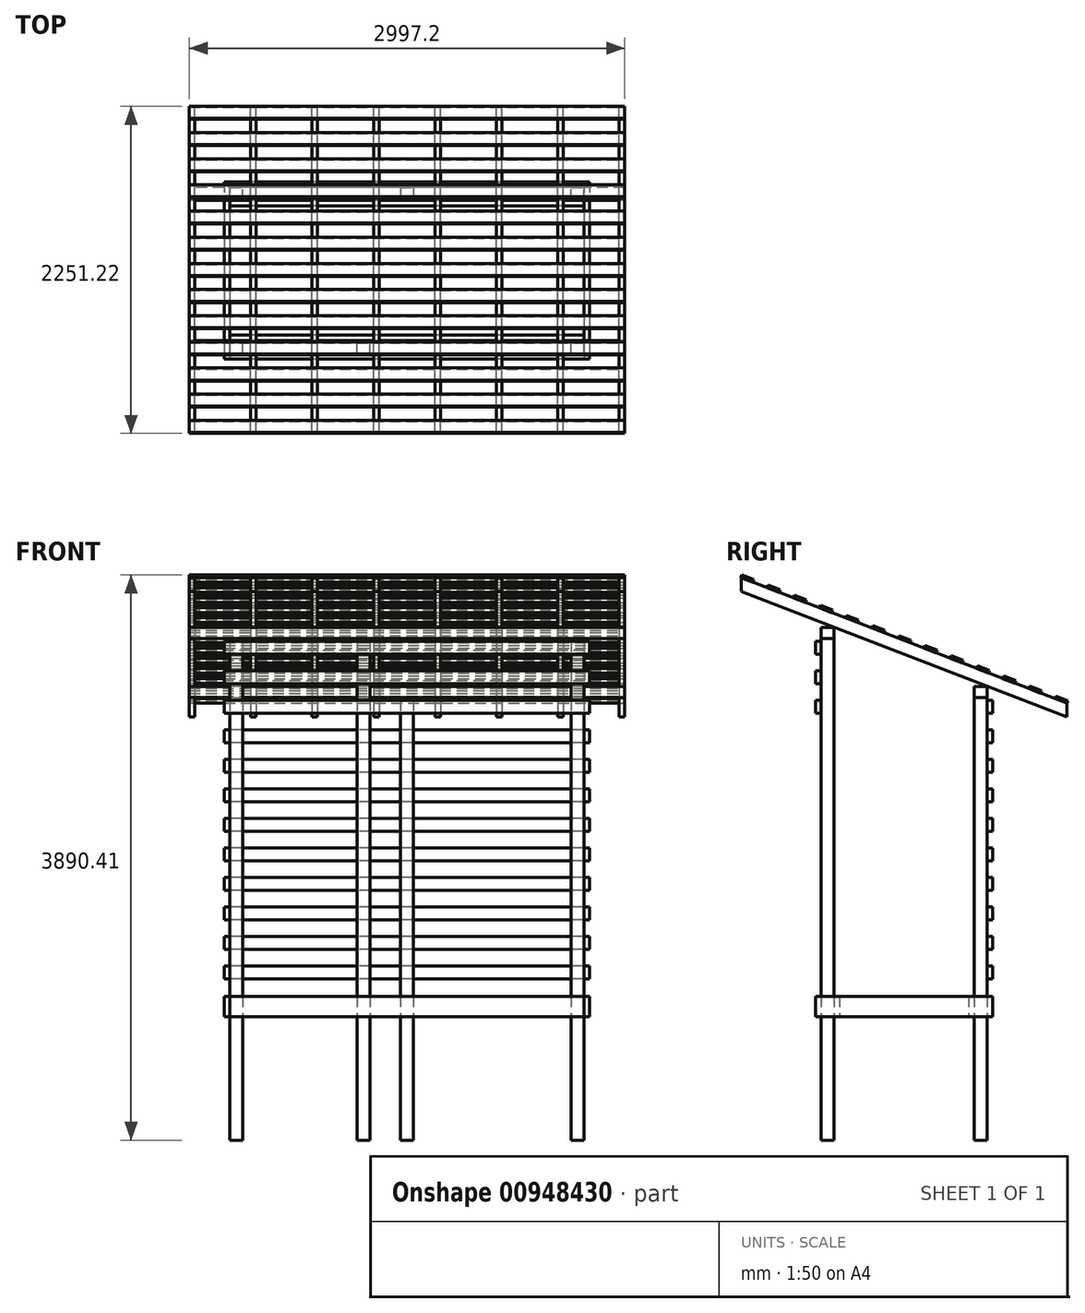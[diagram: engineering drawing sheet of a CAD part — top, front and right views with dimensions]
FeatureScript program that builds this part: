
annotation { "Feature Type Name" : "Feature", "Feature Type Description" : "" }
export const myFeature = defineFeature(function(context is Context, id is Id, definition is map)
    precondition{}
    {
        {
            var Q0;
            Q0=qCreatedBy(makeId("Top.planeOp"),FACE);
            var sketch = newSketch(context, id + "F0", { "sketchPlane" : qUnion([Q0])});
            skLineSegment(sketch, "E0.bottom", {"start": v(0, 0) * mm, "end": v(88.9, 0) * mm});
            skLineSegment(sketch, "E0.top", {"start": v(0, 88.9) * mm, "end": v(88.9, 88.9) * mm});
            skLineSegment(sketch, "E0.left", {"start": v(0, 0) * mm, "end": v(0, 88.9) * mm});
            skLineSegment(sketch, "E0.right", {"start": v(88.9, 0) * mm, "end": v(88.9, 88.9) * mm});
            skLineSegment(sketch, "E1.bottom", {"start": v(2349.5, 0) * mm, "end": v(2438.4, 0) * mm});
            skLineSegment(sketch, "E1.top", {"start": v(2349.5, 88.9) * mm, "end": v(2438.4, 88.9) * mm});
            skLineSegment(sketch, "E1.left", {"start": v(2349.5, 0) * mm, "end": v(2349.5, 88.9) * mm});
            skLineSegment(sketch, "E1.right", {"start": v(2438.4, 0) * mm, "end": v(2438.4, 88.9) * mm});
            skLineSegment(sketch, "E2.bottom", {"start": v(0, 1054.1) * mm, "end": v(88.9, 1054.1) * mm});
            skLineSegment(sketch, "E2.top", {"start": v(0, 1143) * mm, "end": v(88.9, 1143) * mm});
            skLineSegment(sketch, "E2.left", {"start": v(0, 1054.1) * mm, "end": v(0, 1143) * mm});
            skLineSegment(sketch, "E2.right", {"start": v(88.9, 1054.1) * mm, "end": v(88.9, 1143) * mm});
            skLineSegment(sketch, "E3.bottom", {"start": v(2349.5, 1054.1) * mm, "end": v(2438.4, 1054.1) * mm});
            skLineSegment(sketch, "E3.top", {"start": v(2349.5, 1143) * mm, "end": v(2438.4, 1143) * mm});
            skLineSegment(sketch, "E3.left", {"start": v(2349.5, 1054.1) * mm, "end": v(2349.5, 1143) * mm});
            skLineSegment(sketch, "E3.right", {"start": v(2438.4, 1054.1) * mm, "end": v(2438.4, 1143) * mm});
            skLineSegment(sketch, "E4.bottom", {"start": v(876.3, 0) * mm, "end": v(965.2, 0) * mm});
            skLineSegment(sketch, "E4.top", {"start": v(876.3, 88.9) * mm, "end": v(965.2, 88.9) * mm});
            skLineSegment(sketch, "E4.left", {"start": v(876.3, 0) * mm, "end": v(876.3, 88.9) * mm});
            skLineSegment(sketch, "E4.right", {"start": v(965.2, 0) * mm, "end": v(965.2, 88.9) * mm});
            skLineSegment(sketch, "E5.bottom", {"start": v(1174.75, 1143) * mm, "end": v(1263.65, 1143) * mm});
            skLineSegment(sketch, "E5.top", {"start": v(1174.75, 1054.1) * mm, "end": v(1263.65, 1054.1) * mm});
            skLineSegment(sketch, "E5.left", {"start": v(1174.75, 1143) * mm, "end": v(1174.75, 1054.1) * mm});
            skLineSegment(sketch, "E5.right", {"start": v(1263.65, 1143) * mm, "end": v(1263.65, 1054.1) * mm});
            skSolve(sketch);
        }
        {
            var Q0;
            Q0 = qSketchRegion(id + "F0", true);
            var Q1;
            Q1 = qConstructionFilter(qBodyType(qCreatedBy(id + "F0" ,EDGE), BodyType.WIRE), ConstructionObject.NO);
            extrude(context, id + "F1", {"entities" : qUnion([Q0]), "surfaceEntities" : qUnion([Q1]), "depth" : 2667 * mm, "offsetDistance" : 25.4 * mm, "hasSecondDirection" : true, "secondDirectionOppositeDirection" : true, "secondDirectionDepth" : 990.6 * mm});
        }
        {
            var Q0;
            Q0=qCreatedBy(makeId("Right.planeOp"),FACE);
            var sketch = newSketch(context, id + "F2", { "sketchPlane" : qUnion([Q0])});
            skLineSegment(sketch, "E6.bottom", {"start": v(0, 0) * mm, "end": v(-38.1, 0) * mm});
            skLineSegment(sketch, "E6.top", {"start": v(0, -139.7) * mm, "end": v(-38.1, -139.7) * mm});
            skLineSegment(sketch, "E6.left", {"start": v(0, 0) * mm, "end": v(0, -139.7) * mm});
            skLineSegment(sketch, "E6.right", {"start": v(-38.1, 0) * mm, "end": v(-38.1, -139.7) * mm});
            skLineSegment(sketch, "E7.bottom", {"start": v(1143, 0) * mm, "end": v(1181.1, 0) * mm});
            skLineSegment(sketch, "E7.top", {"start": v(1143, -139.7) * mm, "end": v(1181.1, -139.7) * mm});
            skLineSegment(sketch, "E7.left", {"start": v(1143, 0) * mm, "end": v(1143, -139.7) * mm});
            skLineSegment(sketch, "E7.right", {"start": v(1181.1, 0) * mm, "end": v(1181.1, -139.7) * mm});
            skLineSegment(sketch, "E8.bottom", {"start": v(1054.1, 0) * mm, "end": v(1016, 0) * mm});
            skLineSegment(sketch, "E8.top", {"start": v(1054.1, -139.7) * mm, "end": v(1016, -139.7) * mm});
            skLineSegment(sketch, "E8.left", {"start": v(1054.1, 0) * mm, "end": v(1054.1, -139.7) * mm});
            skLineSegment(sketch, "E8.right", {"start": v(1016, 0) * mm, "end": v(1016, -139.7) * mm});
            skLineSegment(sketch, "E9.bottom", {"start": v(127, 0) * mm, "end": v(88.9, 0) * mm});
            skLineSegment(sketch, "E9.top", {"start": v(127, -139.7) * mm, "end": v(88.9, -139.7) * mm});
            skLineSegment(sketch, "E9.left", {"start": v(127, 0) * mm, "end": v(127, -139.7) * mm});
            skLineSegment(sketch, "E9.right", {"start": v(88.9, 0) * mm, "end": v(88.9, -139.7) * mm});
            skSolve(sketch);
        }
        {
            var Q0;
            Q0 = qSketchRegion(id + "F2", true);
            extrude(context, id + "F3", {"entities" : qUnion([Q0]), "depth" : 2438.4 * mm, "offsetDistance" : 25.4 * mm});
        }
        {
            var Q0;
            Q0=makeQuery(id+"F3.opExtrude","SWEPT_FACE",FACE,{"disambiguationData":[OSD([sQuery(id+"F2.wireOp",EDGE,"E6.right")])]});
            var sketch = newSketch(context, id + "F4", { "sketchPlane" : qUnion([Q0])});
            skLineSegment(sketch, "E10.bottom", {"start": v(0, 0) * mm, "end": v(-38.1, 0) * mm});
            skLineSegment(sketch, "E10.top", {"start": v(0, -139.7) * mm, "end": v(-38.1, -139.7) * mm});
            skLineSegment(sketch, "E10.left", {"start": v(0, 0) * mm, "end": v(0, -139.7) * mm});
            skLineSegment(sketch, "E10.right", {"start": v(-38.1, 0) * mm, "end": v(-38.1, -139.7) * mm});
            skLineSegment(sketch, "E11.bottom", {"start": v(2476.5, 0) * mm, "end": v(2438.4, 0) * mm});
            skLineSegment(sketch, "E11.top", {"start": v(2476.5, -139.7) * mm, "end": v(2438.4, -139.7) * mm});
            skLineSegment(sketch, "E11.left", {"start": v(2476.5, 0) * mm, "end": v(2476.5, -139.7) * mm});
            skLineSegment(sketch, "E11.right", {"start": v(2438.4, 0) * mm, "end": v(2438.4, -139.7) * mm});
            skSolve(sketch);
        }
        {
            var Q0;
            Q0 = qSketchRegion(id + "F4", true);
            extrude(context, id + "F5", {"entities" : qUnion([Q0]), "oppositeDirection" : true, "depth" : 1219.2 * mm, "offsetDistance" : 25.4 * mm});
        }
        {
            var Q0;
            Q0=makeQuery(id+"F5.opExtrude","SWEPT_FACE",FACE,{"disambiguationData":[OSD([sQuery(id+"F4.wireOp",EDGE,"E10.right")])]});
            var sketch = newSketch(context, id + "F6", { "sketchPlane" : qUnion([Q0])});
            skLineSegment(sketch, "E12.bottom", {"start": v(-591.38, 2057.4) * mm, "end": v(-1626.38, 2057.4) * mm});
            skLineSegment(sketch, "E12.top", {"start": v(-591.38, 3060.64) * mm, "end": v(-1626.38, 3060.64) * mm});
            skLineSegment(sketch, "E12.left", {"start": v(-591.38, 2057.4) * mm, "end": v(-591.38, 3060.64) * mm});
            skLineSegment(sketch, "E12.right", {"start": v(-1626.38, 2057.4) * mm, "end": v(-1626.38, 3060.64) * mm});
            skLineSegment(sketch, "E13.bottom", {"start": v(182.21, 2463.8) * mm, "end": v(-373.83, 2463.8) * mm});
            skLineSegment(sketch, "E13.top", {"start": v(182.21, 2900.6) * mm, "end": v(-373.83, 2900.6) * mm});
            skLineSegment(sketch, "E13.left", {"start": v(182.21, 2463.8) * mm, "end": v(182.21, 2900.6) * mm});
            skLineSegment(sketch, "E13.right", {"start": v(-373.83, 2463.8) * mm, "end": v(-373.83, 2900.6) * mm});
            skSolve(sketch);
        }
        {
            var Q0;
            Q0 = qSketchRegion(id + "F6", true);
            extrude(context, id + "F7", {"entities" : qUnion([Q0]), "operationType" : NewBodyOperationType.REMOVE, "oppositeDirection" : true, "depth" : 2540 * mm, "offsetDistance" : 25.4 * mm});
        }
        {
            var Q0;
            Q0=makeQuery(id+"F1.opExtrude","SWEPT_FACE",FACE,{"disambiguationData":[OSD([sQuery(id+"F0.wireOp",EDGE,"E2.left")])]});
            cPlane(context, id + "F8", {"entities" : qUnion([Q0]), "cplaneType" : CPlaneType.OFFSET, "offset" : 279.4 * mm, "width" : 152.4 * mm, "height" : 152.4 * mm});
        }
        {
            var Q0;
            Q0=makeQuery(id+"F1.opExtrude","SWEPT_FACE",FACE,{"disambiguationData":[OSD([sQuery(id+"F0.wireOp",EDGE,"E3.right")])]});
            cPlane(context, id + "F9", {"entities" : qUnion([Q0]), "cplaneType" : CPlaneType.OFFSET, "offset" : 279.4 * mm, "width" : 152.4 * mm, "height" : 152.4 * mm});
        }
        {
            var Q0;
            Q0=qCreatedBy(id+"F8.planeOp",FACE);
            var sketch = newSketch(context, id + "F10", { "sketchPlane" : qUnion([Q0])});
            skLineSegment(sketch, "E14.bottom", {"start": v(-1143, 2133.6) * mm, "end": v(-1054.1, 2133.6) * mm});
            skLineSegment(sketch, "E14.top", {"start": v(-1143, 2095.5) * mm, "end": v(-1054.1, 2095.5) * mm});
            skLineSegment(sketch, "E14.left", {"start": v(-1143, 2133.6) * mm, "end": v(-1143, 2095.5) * mm});
            skLineSegment(sketch, "E14.right", {"start": v(-1054.1, 2133.6) * mm, "end": v(-1054.1, 2095.5) * mm});
            skLineSegment(sketch, "E15.top", {"start": v(-1143, 2057.4) * mm, "end": v(-1054.1, 2057.4) * mm});
            skLineSegment(sketch, "E15.left", {"start": v(-1143, 2095.5) * mm, "end": v(-1143, 2057.4) * mm});
            skLineSegment(sketch, "E15.right", {"start": v(-1054.1, 2095.5) * mm, "end": v(-1054.1, 2057.4) * mm});
            skLineSegment(sketch, "E16.bottom", {"start": v(0, 2540) * mm, "end": v(-88.9, 2540) * mm});
            skLineSegment(sketch, "E16.top", {"start": v(0, 2501.9) * mm, "end": v(-88.9, 2501.9) * mm});
            skLineSegment(sketch, "E16.left", {"start": v(0, 2540) * mm, "end": v(0, 2501.9) * mm});
            skLineSegment(sketch, "E16.right", {"start": v(-88.9, 2540) * mm, "end": v(-88.9, 2501.9) * mm});
            skLineSegment(sketch, "E17.top", {"start": v(0, 2463.8) * mm, "end": v(-88.9, 2463.8) * mm});
            skLineSegment(sketch, "E17.left", {"start": v(0, 2501.9) * mm, "end": v(0, 2463.8) * mm});
            skLineSegment(sketch, "E17.right", {"start": v(-88.9, 2501.9) * mm, "end": v(-88.9, 2463.8) * mm});
            skSolve(sketch);
        }
        {
            var Q0;
            Q0 = qSketchRegion(id + "F10", true);
            var Q1;
            Q1=qCreatedBy(id+"F9.planeOp",FACE);
            extrude(context, id + "F11", {"entities" : qUnion([Q0]), "endBound" : BoundingType.UP_TO_SURFACE, "oppositeDirection" : true, "depth" : 25.4 * mm, "endBoundEntityFace" : qUnion([Q1]), "offsetDistance" : 25.4 * mm});
        }
        {
            var Q0;
            Q0=makeQuery(id+"F11.opExtrude","CAP_VERTEX",VERTEX,{"disambiguationData":[OSD([sQuery(id+"F10.wireOp",EDGE,"E14.bottom"),sQuery(id+"F10.wireOp",EDGE,"E14.left"),sQuery(id+"F10.wireOp",EDGE,"E15.left")])],"isStart":false});
            var Q1;
            Q1=makeQuery(id+"F11.opExtrude","CAP_VERTEX",VERTEX,{"disambiguationData":[OSD([sQuery(id+"F10.wireOp",EDGE,"E14.bottom"),sQuery(id+"F10.wireOp",EDGE,"E14.left")])],"isStart":true});
            var Q2;
            Q2=makeQuery(id+"F11.opExtrude","CAP_VERTEX",VERTEX,{"disambiguationData":[OSD([sQuery(id+"F10.wireOp",EDGE,"E16.bottom"),sQuery(id+"F10.wireOp",EDGE,"E16.right")])],"isStart":true});
            cPlane(context, id + "F12", {"entities" : qUnion([Q0, Q1, Q2]), "cplaneType" : CPlaneType.THREE_POINT, "offset" : 25.4 * mm, "width" : 152.4 * mm, "height" : 152.4 * mm});
        }
        {
            var Q0;
            Q0=qCreatedBy(id+"F12.planeOp",FACE);
            var Q1;
            Q1=makeQuery(id+"F11.opExtrude","SWEPT_EDGE",EDGE,{"disambiguationData":[OSD([sQuery(id+"F10.wireOp",EDGE,"E16.bottom"),sQuery(id+"F10.wireOp",EDGE,"E16.right")])]});
            cPlane(context, id + "F13", {"entities" : qUnion([Q0, Q1]), "cplaneType" : CPlaneType.LINE_ANGLE, "offset" : 25.4 * mm, "angle" : 90 * degree, "oppositeDirection" : true, "width" : 152.4 * mm, "height" : 152.4 * mm});
        }
        {
            var Q0;
            Q0=qCreatedBy(id+"F13.planeOp",FACE);
            var sketch = newSketch(context, id + "F14", { "sketchPlane" : qUnion([Q0])});
            skLineSegment(sketch, "E18.bottom", {"start": v(-279.4, 2490.84) * mm, "end": v(-241.3, 2490.84) * mm});
            skLineSegment(sketch, "E18.top", {"start": v(-279.4, 2401.94) * mm, "end": v(-241.3, 2401.94) * mm});
            skLineSegment(sketch, "E18.left", {"start": v(-279.4, 2490.84) * mm, "end": v(-279.4, 2401.94) * mm});
            skLineSegment(sketch, "E18.right", {"start": v(-241.3, 2490.84) * mm, "end": v(-241.3, 2401.94) * mm});
            skLineSegment(sketch, "E19.1.0.0", {"start": v(181.36, 2490.84) * mm, "end": v(181.36, 2401.94) * mm});
            skLineSegment(sketch, "E19.1.0.1", {"start": v(143.26, 2490.84) * mm, "end": v(143.26, 2401.94) * mm});
            skLineSegment(sketch, "E19.1.0.2", {"start": v(143.26, 2490.84) * mm, "end": v(181.36, 2490.84) * mm});
            skLineSegment(sketch, "E19.1.0.3", {"start": v(143.26, 2401.94) * mm, "end": v(181.36, 2401.94) * mm});
            skLineSegment(sketch, "E19.2.0.0", {"start": v(604.01, 2490.84) * mm, "end": v(604.01, 2401.94) * mm});
            skLineSegment(sketch, "E19.2.0.1", {"start": v(565.91, 2490.84) * mm, "end": v(565.91, 2401.94) * mm});
            skLineSegment(sketch, "E19.2.0.2", {"start": v(565.91, 2490.84) * mm, "end": v(604.01, 2490.84) * mm});
            skLineSegment(sketch, "E19.2.0.3", {"start": v(565.91, 2401.94) * mm, "end": v(604.01, 2401.94) * mm});
            skLineSegment(sketch, "E19.3.0.0", {"start": v(1026.67, 2490.84) * mm, "end": v(1026.67, 2401.94) * mm});
            skLineSegment(sketch, "E19.3.0.1", {"start": v(988.57, 2490.84) * mm, "end": v(988.57, 2401.94) * mm});
            skLineSegment(sketch, "E19.3.0.2", {"start": v(988.57, 2490.84) * mm, "end": v(1026.67, 2490.84) * mm});
            skLineSegment(sketch, "E19.3.0.3", {"start": v(988.57, 2401.94) * mm, "end": v(1026.67, 2401.94) * mm});
            skLineSegment(sketch, "E19.4.0.0", {"start": v(1449.32, 2490.84) * mm, "end": v(1449.32, 2401.94) * mm});
            skLineSegment(sketch, "E19.4.0.1", {"start": v(1411.22, 2490.84) * mm, "end": v(1411.22, 2401.94) * mm});
            skLineSegment(sketch, "E19.4.0.2", {"start": v(1411.22, 2490.84) * mm, "end": v(1449.32, 2490.84) * mm});
            skLineSegment(sketch, "E19.4.0.3", {"start": v(1411.22, 2401.94) * mm, "end": v(1449.32, 2401.94) * mm});
            skLineSegment(sketch, "E19.5.0.0", {"start": v(1871.98, 2490.84) * mm, "end": v(1871.98, 2401.94) * mm});
            skLineSegment(sketch, "E19.5.0.1", {"start": v(1833.88, 2490.84) * mm, "end": v(1833.88, 2401.94) * mm});
            skLineSegment(sketch, "E19.5.0.2", {"start": v(1833.88, 2490.84) * mm, "end": v(1871.98, 2490.84) * mm});
            skLineSegment(sketch, "E19.5.0.3", {"start": v(1833.88, 2401.94) * mm, "end": v(1871.98, 2401.94) * mm});
            skLineSegment(sketch, "E19.6.0.0", {"start": v(2294.64, 2490.84) * mm, "end": v(2294.64, 2401.94) * mm});
            skLineSegment(sketch, "E19.6.0.1", {"start": v(2256.54, 2490.84) * mm, "end": v(2256.54, 2401.94) * mm});
            skLineSegment(sketch, "E19.6.0.2", {"start": v(2256.54, 2490.84) * mm, "end": v(2294.64, 2490.84) * mm});
            skLineSegment(sketch, "E19.6.0.3", {"start": v(2256.54, 2401.94) * mm, "end": v(2294.64, 2401.94) * mm});
            skLineSegment(sketch, "E19.7.0.0", {"start": v(2717.3, 2490.84) * mm, "end": v(2717.3, 2401.94) * mm});
            skLineSegment(sketch, "E19.7.0.1", {"start": v(2679.2, 2490.84) * mm, "end": v(2679.2, 2401.94) * mm});
            skLineSegment(sketch, "E19.7.0.2", {"start": v(2679.2, 2490.84) * mm, "end": v(2717.3, 2490.84) * mm});
            skLineSegment(sketch, "E19.7.0.3", {"start": v(2679.2, 2401.94) * mm, "end": v(2717.3, 2401.94) * mm});
            skLineSegment(sketch, "E19.direction1", {"start": v(-279.4, 2401.94) * mm, "end": v(143.26, 2401.94) * mm, "construction": true});
            skSolve(sketch);
        }
        {
            var Q0;
            Q0 = qSketchRegion(id + "F14", true);
            extrude(context, id + "F15", {"entities" : qUnion([Q0]), "depth" : 914.4 * mm, "offsetDistance" : 25.4 * mm, "hasSecondDirection" : true, "secondDirectionOppositeDirection" : true, "secondDirectionDepth" : 2032 * mm});
        }
        {
            var Q0;
            Q0=makeQuery(id+"F15.opExtrude","SWEPT_FACE",FACE,{"disambiguationData":[OSD([sQuery(id+"F14.wireOp",EDGE,"E19.7.0.0")])]});
            var sketch = newSketch(context, id + "F16", { "sketchPlane" : qUnion([Q0])});
            skLineSegment(sketch, "E20.0", {"start": v(-732.3, 2951.89) * mm, "end": v(2016.85, 1891.97) * mm, "construction": true});
            skLineSegment(sketch, "E21.0", {"start": v(-764.29, 2868.94) * mm, "end": v(1984.87, 1809.02) * mm, "construction": true});
            skLineSegment(sketch, "E22.0.1", {"start": v(1984.87, 1809.02) * mm, "end": v(-764.29, 2868.94) * mm, "construction": true});
            skLineSegment(sketch, "E23", {"start": v(-482.62, 3056.48) * mm, "end": v(-582.02, 2798.67) * mm, "construction": true});
            skLineSegment(sketch, "E24", {"start": v(1869.51, 2378.95) * mm, "end": v(1693.15, 1921.5) * mm, "construction": true});
            skLineSegment(sketch, "E25", {"start": v(-550.04, 2881.62) * mm, "end": v(-550.04, 1903.82) * mm, "construction": true});
            skLineSegment(sketch, "E26", {"start": v(1693.15, 1921.5) * mm, "end": v(1693.15, 2626.37) * mm, "construction": true});
            skLineSegment(sketch, "E27.bottom", {"start": v(-550.04, 1903.82) * mm, "end": v(-1357.61, 1903.82) * mm});
            skLineSegment(sketch, "E27.top", {"start": v(-550.04, 3436.76) * mm, "end": v(-1357.61, 3436.76) * mm});
            skLineSegment(sketch, "E27.left", {"start": v(-550.04, 1903.82) * mm, "end": v(-550.04, 3436.76) * mm});
            skLineSegment(sketch, "E27.right", {"start": v(-1357.61, 1903.82) * mm, "end": v(-1357.61, 3436.76) * mm});
            skLineSegment(sketch, "E28.bottom", {"start": v(1693.15, 2626.37) * mm, "end": v(2714.66, 2626.37) * mm});
            skLineSegment(sketch, "E28.top", {"start": v(1693.15, 1154.5) * mm, "end": v(2714.66, 1154.5) * mm});
            skLineSegment(sketch, "E28.left", {"start": v(1693.15, 2626.37) * mm, "end": v(1693.15, 1154.5) * mm});
            skLineSegment(sketch, "E28.right", {"start": v(2714.66, 2626.37) * mm, "end": v(2714.66, 1154.5) * mm});
            skSolve(sketch);
        }
        {
            var Q0;
            Q0 = qSketchRegion(id + "F16", true);
            extrude(context, id + "F17", {"entities" : qUnion([Q0]), "operationType" : NewBodyOperationType.REMOVE, "oppositeDirection" : true, "depth" : 3302 * mm, "offsetDistance" : 25.4 * mm});
        }
        {
            var Q0;
            Q0=makeQuery(id+"F15.opExtrude","SWEPT_FACE",FACE,{"disambiguationData":[OSD([sQuery(id+"F14.wireOp",EDGE,"E19.7.0.0")])]});
            var sketch = newSketch(context, id + "F18", { "sketchPlane" : qUnion([Q0])});
            skLineSegment(sketch, "E29", {"start": v(1693.15, 2016.77) * mm, "end": v(1610.2, 2048.75) * mm});
            skLineSegment(sketch, "E30", {"start": v(1610.2, 2048.75) * mm, "end": v(1617.05, 2066.53) * mm});
            skLineSegment(sketch, "E31", {"start": v(1617.05, 2066.53) * mm, "end": v(1700, 2034.55) * mm});
            skLineSegment(sketch, "E32", {"start": v(1693.15, 2016.77) * mm, "end": v(1700, 2034.55) * mm});
            skLineSegment(sketch, "E33", {"start": v(-550.04, 2881.62) * mm, "end": v(1693.15, 2016.77) * mm, "construction": true});
            skLineSegment(sketch, "E34.1.0.0", {"start": v(1513.03, 2086.21) * mm, "end": v(1430.08, 2118.2) * mm});
            skLineSegment(sketch, "E34.1.0.1", {"start": v(1436.93, 2135.97) * mm, "end": v(1519.88, 2103.99) * mm});
            skLineSegment(sketch, "E34.1.0.2", {"start": v(1430.08, 2118.2) * mm, "end": v(1436.93, 2135.97) * mm});
            skLineSegment(sketch, "E34.1.0.3", {"start": v(1513.03, 2086.21) * mm, "end": v(1519.88, 2103.99) * mm});
            skLineSegment(sketch, "E34.2.0.0", {"start": v(1332.9, 2155.65) * mm, "end": v(1249.96, 2187.63) * mm});
            skLineSegment(sketch, "E34.2.0.1", {"start": v(1256.81, 2205.4) * mm, "end": v(1339.76, 2173.43) * mm});
            skLineSegment(sketch, "E34.2.0.2", {"start": v(1249.96, 2187.63) * mm, "end": v(1256.81, 2205.4) * mm});
            skLineSegment(sketch, "E34.2.0.3", {"start": v(1332.9, 2155.65) * mm, "end": v(1339.76, 2173.43) * mm});
            skLineSegment(sketch, "E34.3.0.0", {"start": v(1152.8, 2225.1) * mm, "end": v(1069.84, 2257.07) * mm});
            skLineSegment(sketch, "E34.3.0.1", {"start": v(1076.7, 2274.85) * mm, "end": v(1159.64, 2242.87) * mm});
            skLineSegment(sketch, "E34.3.0.2", {"start": v(1069.84, 2257.07) * mm, "end": v(1076.7, 2274.85) * mm});
            skLineSegment(sketch, "E34.3.0.3", {"start": v(1152.8, 2225.1) * mm, "end": v(1159.64, 2242.87) * mm});
            skLineSegment(sketch, "E34.4.0.0", {"start": v(972.67, 2294.53) * mm, "end": v(889.72, 2326.52) * mm});
            skLineSegment(sketch, "E34.4.0.1", {"start": v(896.58, 2344.29) * mm, "end": v(979.53, 2312.3) * mm});
            skLineSegment(sketch, "E34.4.0.2", {"start": v(889.72, 2326.52) * mm, "end": v(896.58, 2344.29) * mm});
            skLineSegment(sketch, "E34.4.0.3", {"start": v(972.67, 2294.53) * mm, "end": v(979.53, 2312.3) * mm});
            skLineSegment(sketch, "E34.5.0.0", {"start": v(792.56, 2363.98) * mm, "end": v(709.6, 2395.96) * mm});
            skLineSegment(sketch, "E34.5.0.1", {"start": v(716.46, 2413.73) * mm, "end": v(799.4, 2381.75) * mm});
            skLineSegment(sketch, "E34.5.0.2", {"start": v(709.6, 2395.96) * mm, "end": v(716.46, 2413.73) * mm});
            skLineSegment(sketch, "E34.5.0.3", {"start": v(792.56, 2363.98) * mm, "end": v(799.4, 2381.75) * mm});
            skLineSegment(sketch, "E34.6.0.0", {"start": v(612.44, 2433.42) * mm, "end": v(529.49, 2465.4) * mm});
            skLineSegment(sketch, "E34.6.0.1", {"start": v(536.34, 2483.17) * mm, "end": v(619.3, 2451.2) * mm});
            skLineSegment(sketch, "E34.6.0.2", {"start": v(529.49, 2465.4) * mm, "end": v(536.34, 2483.17) * mm});
            skLineSegment(sketch, "E34.6.0.3", {"start": v(612.44, 2433.42) * mm, "end": v(619.3, 2451.2) * mm});
            skLineSegment(sketch, "E34.7.0.0", {"start": v(432.32, 2502.86) * mm, "end": v(349.37, 2534.84) * mm});
            skLineSegment(sketch, "E34.7.0.1", {"start": v(356.22, 2552.61) * mm, "end": v(439.17, 2520.63) * mm});
            skLineSegment(sketch, "E34.7.0.2", {"start": v(349.37, 2534.84) * mm, "end": v(356.22, 2552.61) * mm});
            skLineSegment(sketch, "E34.7.0.3", {"start": v(432.32, 2502.86) * mm, "end": v(439.17, 2520.63) * mm});
            skLineSegment(sketch, "E34.8.0.0", {"start": v(252.2, 2572.3) * mm, "end": v(169.25, 2604.28) * mm});
            skLineSegment(sketch, "E34.8.0.1", {"start": v(176.1, 2622.05) * mm, "end": v(259.05, 2590.07) * mm});
            skLineSegment(sketch, "E34.8.0.2", {"start": v(169.25, 2604.28) * mm, "end": v(176.1, 2622.05) * mm});
            skLineSegment(sketch, "E34.8.0.3", {"start": v(252.2, 2572.3) * mm, "end": v(259.05, 2590.07) * mm});
            skLineSegment(sketch, "E34.9.0.0", {"start": v(72.08, 2641.74) * mm, "end": v(-10.87, 2673.72) * mm});
            skLineSegment(sketch, "E34.9.0.1", {"start": v(-4.01, 2691.5) * mm, "end": v(78.94, 2659.51) * mm});
            skLineSegment(sketch, "E34.9.0.2", {"start": v(-10.87, 2673.72) * mm, "end": v(-4.01, 2691.5) * mm});
            skLineSegment(sketch, "E34.9.0.3", {"start": v(72.08, 2641.74) * mm, "end": v(78.94, 2659.51) * mm});
            skLineSegment(sketch, "E34.10.0.0", {"start": v(-108.03, 2711.18) * mm, "end": v(-190.98, 2743.16) * mm});
            skLineSegment(sketch, "E34.10.0.1", {"start": v(-184.13, 2760.93) * mm, "end": v(-101.18, 2728.95) * mm});
            skLineSegment(sketch, "E34.10.0.2", {"start": v(-190.98, 2743.16) * mm, "end": v(-184.13, 2760.93) * mm});
            skLineSegment(sketch, "E34.10.0.3", {"start": v(-108.03, 2711.18) * mm, "end": v(-101.18, 2728.95) * mm});
            skLineSegment(sketch, "E34.11.0.0", {"start": v(-288.15, 2780.62) * mm, "end": v(-371.1, 2812.6) * mm});
            skLineSegment(sketch, "E34.11.0.1", {"start": v(-364.25, 2830.37) * mm, "end": v(-281.3, 2798.4) * mm});
            skLineSegment(sketch, "E34.11.0.2", {"start": v(-371.1, 2812.6) * mm, "end": v(-364.25, 2830.37) * mm});
            skLineSegment(sketch, "E34.11.0.3", {"start": v(-288.15, 2780.62) * mm, "end": v(-281.3, 2798.4) * mm});
            skLineSegment(sketch, "E34.12.0.0", {"start": v(-468.27, 2850.06) * mm, "end": v(-551.22, 2882.04) * mm});
            skLineSegment(sketch, "E34.12.0.1", {"start": v(-544.37, 2899.81) * mm, "end": v(-461.42, 2867.83) * mm});
            skLineSegment(sketch, "E34.12.0.2", {"start": v(-551.22, 2882.04) * mm, "end": v(-544.37, 2899.81) * mm});
            skLineSegment(sketch, "E34.12.0.3", {"start": v(-468.27, 2850.06) * mm, "end": v(-461.42, 2867.83) * mm});
            skLineSegment(sketch, "E34.direction1", {"start": v(1610.2, 2048.75) * mm, "end": v(1430.08, 2118.2) * mm, "construction": true});
            skSolve(sketch);
        }
        {
            var Q0;
            Q0 = qSketchRegion(id + "F18", true);
            var Q1;
            Q1=makeQuery(id+"F15.opExtrude","SWEPT_FACE",FACE,{"disambiguationData":[OSD([sQuery(id+"F14.wireOp",EDGE,"E18.left")])]});
            extrude(context, id + "F19", {"entities" : qUnion([Q0]), "endBound" : BoundingType.UP_TO_SURFACE, "oppositeDirection" : true, "depth" : 25.4 * mm, "endBoundEntityFace" : qUnion([Q1]), "offsetDistance" : 25.4 * mm});
        }
        {
            var Q0;
            Q0=makeQuery(id+"F5.opExtrude","SWEPT_FACE",FACE,{"disambiguationData":[OSD([sQuery(id+"F4.wireOp",EDGE,"E10.right")])]});
            var sketch = newSketch(context, id + "F20", { "sketchPlane" : qUnion([Q0])});
            skLineSegment(sketch, "E35.bottom", {"start": v(-1181.1, 2038.35) * mm, "end": v(-1143, 2038.35) * mm});
            skLineSegment(sketch, "E35.top", {"start": v(-1181.1, 1949.45) * mm, "end": v(-1143, 1949.45) * mm});
            skLineSegment(sketch, "E35.left", {"start": v(-1181.1, 2038.35) * mm, "end": v(-1181.1, 1949.45) * mm});
            skLineSegment(sketch, "E35.right", {"start": v(-1143, 2038.35) * mm, "end": v(-1143, 1949.45) * mm});
            skLineSegment(sketch, "E36.bottom", {"start": v(38.1, 2038.35) * mm, "end": v(0, 2038.35) * mm});
            skLineSegment(sketch, "E36.top", {"start": v(38.1, 1949.45) * mm, "end": v(0, 1949.45) * mm});
            skLineSegment(sketch, "E36.left", {"start": v(38.1, 2038.35) * mm, "end": v(38.1, 1949.45) * mm});
            skLineSegment(sketch, "E36.right", {"start": v(0, 2038.35) * mm, "end": v(0, 1949.45) * mm});
            skLineSegment(sketch, "E37.0.1.0", {"start": v(-1181.1, 1835.15) * mm, "end": v(-1181.1, 1746.25) * mm});
            skLineSegment(sketch, "E37.0.1.1", {"start": v(-1143, 1835.15) * mm, "end": v(-1143, 1746.25) * mm});
            skLineSegment(sketch, "E37.0.1.2", {"start": v(-1181.1, 1835.15) * mm, "end": v(-1143, 1835.15) * mm});
            skLineSegment(sketch, "E37.0.1.3", {"start": v(-1181.1, 1746.25) * mm, "end": v(-1143, 1746.25) * mm});
            skLineSegment(sketch, "E37.0.2.0", {"start": v(-1181.1, 1631.95) * mm, "end": v(-1181.1, 1543.05) * mm});
            skLineSegment(sketch, "E37.0.2.1", {"start": v(-1143, 1631.95) * mm, "end": v(-1143, 1543.05) * mm});
            skLineSegment(sketch, "E37.0.2.2", {"start": v(-1181.1, 1631.95) * mm, "end": v(-1143, 1631.95) * mm});
            skLineSegment(sketch, "E37.0.2.3", {"start": v(-1181.1, 1543.05) * mm, "end": v(-1143, 1543.05) * mm});
            skLineSegment(sketch, "E37.0.3.0", {"start": v(-1181.1, 1428.75) * mm, "end": v(-1181.1, 1339.85) * mm});
            skLineSegment(sketch, "E37.0.3.1", {"start": v(-1143, 1428.75) * mm, "end": v(-1143, 1339.85) * mm});
            skLineSegment(sketch, "E37.0.3.2", {"start": v(-1181.1, 1428.75) * mm, "end": v(-1143, 1428.75) * mm});
            skLineSegment(sketch, "E37.0.3.3", {"start": v(-1181.1, 1339.85) * mm, "end": v(-1143, 1339.85) * mm});
            skLineSegment(sketch, "E37.0.4.0", {"start": v(-1181.1, 1225.55) * mm, "end": v(-1181.1, 1136.65) * mm});
            skLineSegment(sketch, "E37.0.4.1", {"start": v(-1143, 1225.55) * mm, "end": v(-1143, 1136.65) * mm});
            skLineSegment(sketch, "E37.0.4.2", {"start": v(-1181.1, 1225.55) * mm, "end": v(-1143, 1225.55) * mm});
            skLineSegment(sketch, "E37.0.4.3", {"start": v(-1181.1, 1136.65) * mm, "end": v(-1143, 1136.65) * mm});
            skLineSegment(sketch, "E37.0.5.0", {"start": v(-1181.1, 1022.35) * mm, "end": v(-1181.1, 933.45) * mm});
            skLineSegment(sketch, "E37.0.5.1", {"start": v(-1143, 1022.35) * mm, "end": v(-1143, 933.45) * mm});
            skLineSegment(sketch, "E37.0.5.2", {"start": v(-1181.1, 1022.35) * mm, "end": v(-1143, 1022.35) * mm});
            skLineSegment(sketch, "E37.0.5.3", {"start": v(-1181.1, 933.45) * mm, "end": v(-1143, 933.45) * mm});
            skLineSegment(sketch, "E37.0.6.0", {"start": v(-1181.1, 819.15) * mm, "end": v(-1181.1, 730.25) * mm});
            skLineSegment(sketch, "E37.0.6.1", {"start": v(-1143, 819.15) * mm, "end": v(-1143, 730.25) * mm});
            skLineSegment(sketch, "E37.0.6.2", {"start": v(-1181.1, 819.15) * mm, "end": v(-1143, 819.15) * mm});
            skLineSegment(sketch, "E37.0.6.3", {"start": v(-1181.1, 730.25) * mm, "end": v(-1143, 730.25) * mm});
            skLineSegment(sketch, "E37.0.7.0", {"start": v(-1181.1, 615.95) * mm, "end": v(-1181.1, 527.05) * mm});
            skLineSegment(sketch, "E37.0.7.1", {"start": v(-1143, 615.95) * mm, "end": v(-1143, 527.05) * mm});
            skLineSegment(sketch, "E37.0.7.2", {"start": v(-1181.1, 615.95) * mm, "end": v(-1143, 615.95) * mm});
            skLineSegment(sketch, "E37.0.7.3", {"start": v(-1181.1, 527.05) * mm, "end": v(-1143, 527.05) * mm});
            skLineSegment(sketch, "E37.0.8.0", {"start": v(-1181.1, 412.75) * mm, "end": v(-1181.1, 323.85) * mm});
            skLineSegment(sketch, "E37.0.8.1", {"start": v(-1143, 412.75) * mm, "end": v(-1143, 323.85) * mm});
            skLineSegment(sketch, "E37.0.8.2", {"start": v(-1181.1, 412.75) * mm, "end": v(-1143, 412.75) * mm});
            skLineSegment(sketch, "E37.0.8.3", {"start": v(-1181.1, 323.85) * mm, "end": v(-1143, 323.85) * mm});
            skLineSegment(sketch, "E37.0.9.0", {"start": v(-1181.1, 209.55) * mm, "end": v(-1181.1, 120.65) * mm});
            skLineSegment(sketch, "E37.0.9.1", {"start": v(-1143, 209.55) * mm, "end": v(-1143, 120.65) * mm});
            skLineSegment(sketch, "E37.0.9.2", {"start": v(-1181.1, 209.55) * mm, "end": v(-1143, 209.55) * mm});
            skLineSegment(sketch, "E37.0.9.3", {"start": v(-1181.1, 120.65) * mm, "end": v(-1143, 120.65) * mm});
            skLineSegment(sketch, "E37.1.1.0", {"start": v(-1181.1, 1835.15) * mm, "end": v(-1181.1, 1746.25) * mm});
            skLineSegment(sketch, "E37.1.1.1", {"start": v(-1143, 1835.15) * mm, "end": v(-1143, 1746.25) * mm});
            skLineSegment(sketch, "E37.1.1.2", {"start": v(-1181.1, 1835.15) * mm, "end": v(-1143, 1835.15) * mm});
            skLineSegment(sketch, "E37.1.1.3", {"start": v(-1181.1, 1746.25) * mm, "end": v(-1143, 1746.25) * mm});
            skLineSegment(sketch, "E37.1.2.0", {"start": v(-1181.1, 1631.95) * mm, "end": v(-1181.1, 1543.05) * mm});
            skLineSegment(sketch, "E37.1.2.1", {"start": v(-1143, 1631.95) * mm, "end": v(-1143, 1543.05) * mm});
            skLineSegment(sketch, "E37.1.2.2", {"start": v(-1181.1, 1631.95) * mm, "end": v(-1143, 1631.95) * mm});
            skLineSegment(sketch, "E37.1.2.3", {"start": v(-1181.1, 1543.05) * mm, "end": v(-1143, 1543.05) * mm});
            skLineSegment(sketch, "E37.1.3.0", {"start": v(-1181.1, 1428.75) * mm, "end": v(-1181.1, 1339.85) * mm});
            skLineSegment(sketch, "E37.1.3.1", {"start": v(-1143, 1428.75) * mm, "end": v(-1143, 1339.85) * mm});
            skLineSegment(sketch, "E37.1.3.2", {"start": v(-1181.1, 1428.75) * mm, "end": v(-1143, 1428.75) * mm});
            skLineSegment(sketch, "E37.1.3.3", {"start": v(-1181.1, 1339.85) * mm, "end": v(-1143, 1339.85) * mm});
            skLineSegment(sketch, "E37.1.4.0", {"start": v(-1181.1, 1225.55) * mm, "end": v(-1181.1, 1136.65) * mm});
            skLineSegment(sketch, "E37.1.4.1", {"start": v(-1143, 1225.55) * mm, "end": v(-1143, 1136.65) * mm});
            skLineSegment(sketch, "E37.1.4.2", {"start": v(-1181.1, 1225.55) * mm, "end": v(-1143, 1225.55) * mm});
            skLineSegment(sketch, "E37.1.4.3", {"start": v(-1181.1, 1136.65) * mm, "end": v(-1143, 1136.65) * mm});
            skLineSegment(sketch, "E37.1.5.0", {"start": v(-1181.1, 1022.35) * mm, "end": v(-1181.1, 933.45) * mm});
            skLineSegment(sketch, "E37.1.5.1", {"start": v(-1143, 1022.35) * mm, "end": v(-1143, 933.45) * mm});
            skLineSegment(sketch, "E37.1.5.2", {"start": v(-1181.1, 1022.35) * mm, "end": v(-1143, 1022.35) * mm});
            skLineSegment(sketch, "E37.1.5.3", {"start": v(-1181.1, 933.45) * mm, "end": v(-1143, 933.45) * mm});
            skLineSegment(sketch, "E37.1.6.0", {"start": v(-1181.1, 819.15) * mm, "end": v(-1181.1, 730.25) * mm});
            skLineSegment(sketch, "E37.1.6.1", {"start": v(-1143, 819.15) * mm, "end": v(-1143, 730.25) * mm});
            skLineSegment(sketch, "E37.1.6.2", {"start": v(-1181.1, 819.15) * mm, "end": v(-1143, 819.15) * mm});
            skLineSegment(sketch, "E37.1.6.3", {"start": v(-1181.1, 730.25) * mm, "end": v(-1143, 730.25) * mm});
            skLineSegment(sketch, "E37.1.7.0", {"start": v(-1181.1, 615.95) * mm, "end": v(-1181.1, 527.05) * mm});
            skLineSegment(sketch, "E37.1.7.1", {"start": v(-1143, 615.95) * mm, "end": v(-1143, 527.05) * mm});
            skLineSegment(sketch, "E37.1.7.2", {"start": v(-1181.1, 615.95) * mm, "end": v(-1143, 615.95) * mm});
            skLineSegment(sketch, "E37.1.7.3", {"start": v(-1181.1, 527.05) * mm, "end": v(-1143, 527.05) * mm});
            skLineSegment(sketch, "E37.1.8.0", {"start": v(-1181.1, 412.75) * mm, "end": v(-1181.1, 323.85) * mm});
            skLineSegment(sketch, "E37.1.8.1", {"start": v(-1143, 412.75) * mm, "end": v(-1143, 323.85) * mm});
            skLineSegment(sketch, "E37.1.8.2", {"start": v(-1181.1, 412.75) * mm, "end": v(-1143, 412.75) * mm});
            skLineSegment(sketch, "E37.1.8.3", {"start": v(-1181.1, 323.85) * mm, "end": v(-1143, 323.85) * mm});
            skLineSegment(sketch, "E37.1.9.0", {"start": v(-1181.1, 209.55) * mm, "end": v(-1181.1, 120.65) * mm});
            skLineSegment(sketch, "E37.1.9.1", {"start": v(-1143, 209.55) * mm, "end": v(-1143, 120.65) * mm});
            skLineSegment(sketch, "E37.1.9.2", {"start": v(-1181.1, 209.55) * mm, "end": v(-1143, 209.55) * mm});
            skLineSegment(sketch, "E37.1.9.3", {"start": v(-1181.1, 120.65) * mm, "end": v(-1143, 120.65) * mm});
            skLineSegment(sketch, "E37.2.1.0", {"start": v(-1181.1, 1835.15) * mm, "end": v(-1181.1, 1746.25) * mm});
            skLineSegment(sketch, "E37.2.1.1", {"start": v(-1143, 1835.15) * mm, "end": v(-1143, 1746.25) * mm});
            skLineSegment(sketch, "E37.2.1.2", {"start": v(-1181.1, 1835.15) * mm, "end": v(-1143, 1835.15) * mm});
            skLineSegment(sketch, "E37.2.1.3", {"start": v(-1181.1, 1746.25) * mm, "end": v(-1143, 1746.25) * mm});
            skLineSegment(sketch, "E37.2.2.0", {"start": v(-1181.1, 1631.95) * mm, "end": v(-1181.1, 1543.05) * mm});
            skLineSegment(sketch, "E37.2.2.1", {"start": v(-1143, 1631.95) * mm, "end": v(-1143, 1543.05) * mm});
            skLineSegment(sketch, "E37.2.2.2", {"start": v(-1181.1, 1631.95) * mm, "end": v(-1143, 1631.95) * mm});
            skLineSegment(sketch, "E37.2.2.3", {"start": v(-1181.1, 1543.05) * mm, "end": v(-1143, 1543.05) * mm});
            skLineSegment(sketch, "E37.2.3.0", {"start": v(-1181.1, 1428.75) * mm, "end": v(-1181.1, 1339.85) * mm});
            skLineSegment(sketch, "E37.2.3.1", {"start": v(-1143, 1428.75) * mm, "end": v(-1143, 1339.85) * mm});
            skLineSegment(sketch, "E37.2.3.2", {"start": v(-1181.1, 1428.75) * mm, "end": v(-1143, 1428.75) * mm});
            skLineSegment(sketch, "E37.2.3.3", {"start": v(-1181.1, 1339.85) * mm, "end": v(-1143, 1339.85) * mm});
            skLineSegment(sketch, "E37.2.4.0", {"start": v(-1181.1, 1225.55) * mm, "end": v(-1181.1, 1136.65) * mm});
            skLineSegment(sketch, "E37.2.4.1", {"start": v(-1143, 1225.55) * mm, "end": v(-1143, 1136.65) * mm});
            skLineSegment(sketch, "E37.2.4.2", {"start": v(-1181.1, 1225.55) * mm, "end": v(-1143, 1225.55) * mm});
            skLineSegment(sketch, "E37.2.4.3", {"start": v(-1181.1, 1136.65) * mm, "end": v(-1143, 1136.65) * mm});
            skLineSegment(sketch, "E37.2.5.0", {"start": v(-1181.1, 1022.35) * mm, "end": v(-1181.1, 933.45) * mm});
            skLineSegment(sketch, "E37.2.5.1", {"start": v(-1143, 1022.35) * mm, "end": v(-1143, 933.45) * mm});
            skLineSegment(sketch, "E37.2.5.2", {"start": v(-1181.1, 1022.35) * mm, "end": v(-1143, 1022.35) * mm});
            skLineSegment(sketch, "E37.2.5.3", {"start": v(-1181.1, 933.45) * mm, "end": v(-1143, 933.45) * mm});
            skLineSegment(sketch, "E37.2.6.0", {"start": v(-1181.1, 819.15) * mm, "end": v(-1181.1, 730.25) * mm});
            skLineSegment(sketch, "E37.2.6.1", {"start": v(-1143, 819.15) * mm, "end": v(-1143, 730.25) * mm});
            skLineSegment(sketch, "E37.2.6.2", {"start": v(-1181.1, 819.15) * mm, "end": v(-1143, 819.15) * mm});
            skLineSegment(sketch, "E37.2.6.3", {"start": v(-1181.1, 730.25) * mm, "end": v(-1143, 730.25) * mm});
            skLineSegment(sketch, "E37.2.7.0", {"start": v(-1181.1, 615.95) * mm, "end": v(-1181.1, 527.05) * mm});
            skLineSegment(sketch, "E37.2.7.1", {"start": v(-1143, 615.95) * mm, "end": v(-1143, 527.05) * mm});
            skLineSegment(sketch, "E37.2.7.2", {"start": v(-1181.1, 615.95) * mm, "end": v(-1143, 615.95) * mm});
            skLineSegment(sketch, "E37.2.7.3", {"start": v(-1181.1, 527.05) * mm, "end": v(-1143, 527.05) * mm});
            skLineSegment(sketch, "E37.2.8.0", {"start": v(-1181.1, 412.75) * mm, "end": v(-1181.1, 323.85) * mm});
            skLineSegment(sketch, "E37.2.8.1", {"start": v(-1143, 412.75) * mm, "end": v(-1143, 323.85) * mm});
            skLineSegment(sketch, "E37.2.8.2", {"start": v(-1181.1, 412.75) * mm, "end": v(-1143, 412.75) * mm});
            skLineSegment(sketch, "E37.2.8.3", {"start": v(-1181.1, 323.85) * mm, "end": v(-1143, 323.85) * mm});
            skLineSegment(sketch, "E37.2.9.0", {"start": v(-1181.1, 209.55) * mm, "end": v(-1181.1, 120.65) * mm});
            skLineSegment(sketch, "E37.2.9.1", {"start": v(-1143, 209.55) * mm, "end": v(-1143, 120.65) * mm});
            skLineSegment(sketch, "E37.2.9.2", {"start": v(-1181.1, 209.55) * mm, "end": v(-1143, 209.55) * mm});
            skLineSegment(sketch, "E37.2.9.3", {"start": v(-1181.1, 120.65) * mm, "end": v(-1143, 120.65) * mm});
            skLineSegment(sketch, "E37.direction1", {"start": v(-1181.1, 1949.45) * mm, "end": v(-1181.1, 1949.45) * mm});
            skLineSegment(sketch, "E37.direction2", {"start": v(-1181.1, 1949.45) * mm, "end": v(-1181.1, 1746.25) * mm, "construction": true});
            skLineSegment(sketch, "E38.0.1.0", {"start": v(0, 2241.55) * mm, "end": v(0, 2152.65) * mm});
            skLineSegment(sketch, "E38.0.1.1", {"start": v(38.1, 2241.55) * mm, "end": v(38.1, 2152.65) * mm});
            skLineSegment(sketch, "E38.0.1.2", {"start": v(38.1, 2241.55) * mm, "end": v(0, 2241.55) * mm});
            skLineSegment(sketch, "E38.0.1.3", {"start": v(38.1, 2152.65) * mm, "end": v(0, 2152.65) * mm});
            skLineSegment(sketch, "E38.0.2.0", {"start": v(0, 2444.75) * mm, "end": v(0, 2355.85) * mm});
            skLineSegment(sketch, "E38.0.2.1", {"start": v(38.1, 2444.75) * mm, "end": v(38.1, 2355.85) * mm});
            skLineSegment(sketch, "E38.0.2.2", {"start": v(38.1, 2444.75) * mm, "end": v(0, 2444.75) * mm});
            skLineSegment(sketch, "E38.0.2.3", {"start": v(38.1, 2355.85) * mm, "end": v(0, 2355.85) * mm});
            skLineSegment(sketch, "E38.direction1", {"start": v(0, 1949.45) * mm, "end": v(25.4, 1949.45) * mm, "construction": true});
            skLineSegment(sketch, "E38.direction2", {"start": v(0, 1949.45) * mm, "end": v(0, 2152.65) * mm, "construction": true});
            skSolve(sketch);
        }
        {
            var Q0;
            Q0 = qSketchRegion(id + "F20", true);
            var Q1;
            Q1=makeQuery(id+"F5.opExtrude","SWEPT_FACE",FACE,{"disambiguationData":[OSD([sQuery(id+"F4.wireOp",EDGE,"E11.left")])]});
            extrude(context, id + "F21", {"entities" : qUnion([Q0]), "endBound" : BoundingType.UP_TO_SURFACE, "oppositeDirection" : true, "depth" : 25.4 * mm, "endBoundEntityFace" : qUnion([Q1]), "offsetDistance" : 25.4 * mm});
        }
    });
